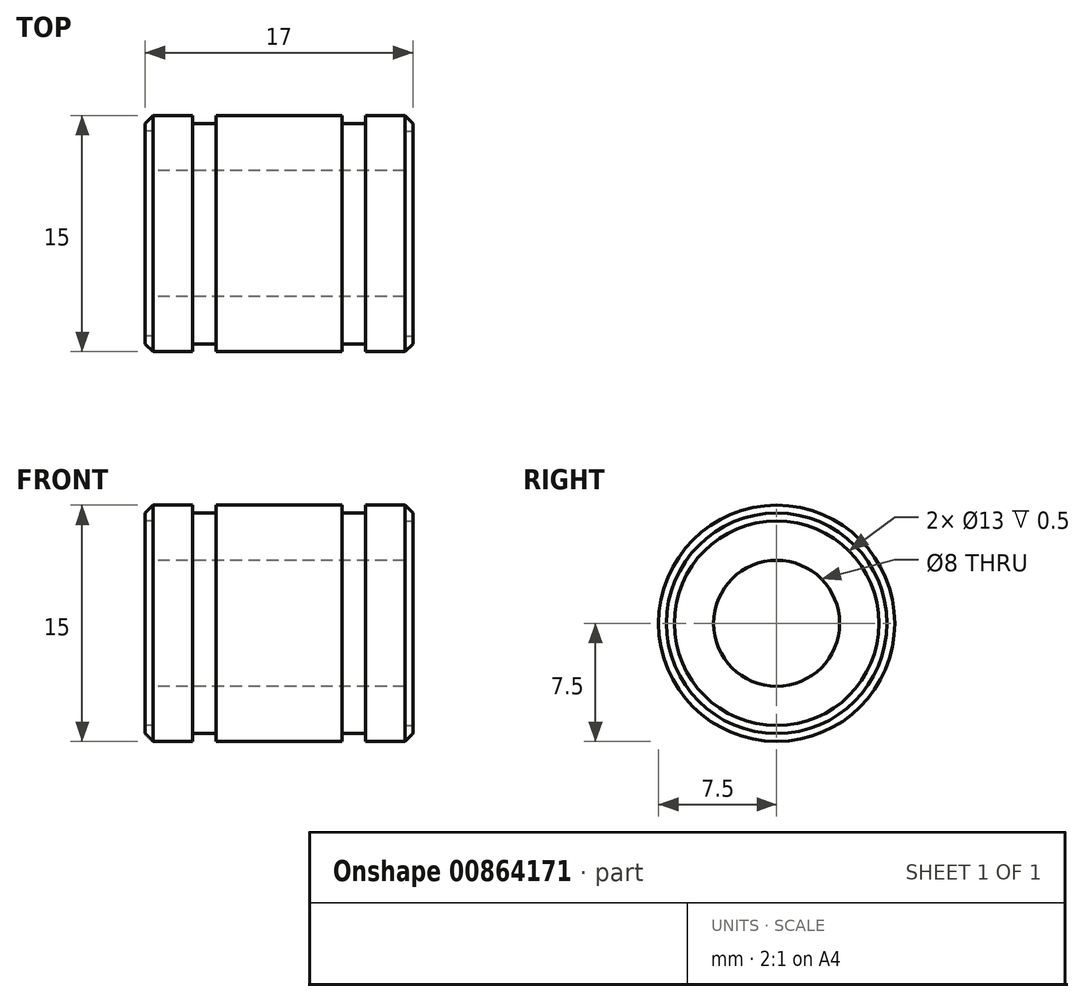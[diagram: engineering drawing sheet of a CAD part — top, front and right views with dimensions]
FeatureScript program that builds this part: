
annotation { "Feature Type Name" : "Feature", "Feature Type Description" : "" }
export const myFeature = defineFeature(function(context is Context, id is Id, definition is map)
    precondition{}
    {
        {
            var Q0;
            Q0=qCreatedBy(makeId("Right.planeOp"),FACE);
            var sketch = newSketch(context, id + "F0", { "sketchPlane" : qUnion([Q0])});
            skCircle(sketch, "E0", {"center": v(0, 0) * mm, "radius": 4 * mm});
            skCircle(sketch, "E1", {"center": v(0, 0) * mm, "radius": 7.5 * mm});
            skSolve(sketch);
        }
        {
            var Q0;
            Q0 = qSketchRegion(id + "F0", true);
            extrude(context, id + "F1", {"entities" : qUnion([Q0]), "endBound" : BoundingType.SYMMETRIC, "depth" : 17 * mm, "offsetDistance" : 25 * mm});
        }
        {
            var Q0;
            Q0=makeQuery(id+"F1.opExtrude","CAP_FACE",FACE,{"disambiguationData":[OSD([sQuery(id+"F0.wireOp",EDGE,"E0"),sQuery(id+"F0.wireOp",EDGE,"E1")])],"isStart":false});
            var sketch = newSketch(context, id + "F2", { "sketchPlane" : qUnion([Q0])});
            skCircle(sketch, "E2", {"center": v(0, 0) * mm, "radius": 6.5 * mm});
            skSolve(sketch);
        }
        {
            var Q0;
            Q0 = qSketchRegion(id + "F2", true);
            extrude(context, id + "F3", {"entities" : qUnion([Q0]), "operationType" : NewBodyOperationType.REMOVE, "oppositeDirection" : true, "depth" : .5 * mm, "offsetDistance" : 25 * mm});
        }
        {
            var Q0;
            Q0=makeQuery(id+"F1.opExtrude","CAP_FACE",FACE,{"disambiguationData":[OSD([sQuery(id+"F0.wireOp",EDGE,"E0"),sQuery(id+"F0.wireOp",EDGE,"E1")])],"isStart":true});
            var sketch = newSketch(context, id + "F4", { "sketchPlane" : qUnion([Q0])});
            skCircle(sketch, "E3", {"center": v(0, 0) * mm, "radius": 6.5 * mm});
            skSolve(sketch);
        }
        {
            var Q0;
            Q0 = qSketchRegion(id + "F4", true);
            extrude(context, id + "F5", {"entities" : qUnion([Q0]), "operationType" : NewBodyOperationType.REMOVE, "oppositeDirection" : true, "depth" : .5 * mm, "offsetDistance" : 25 * mm});
        }
        {
            var Q0;
            Q0=qCreatedBy(makeId("Front.planeOp"),FACE);
            var sketch = newSketch(context, id + "F6", { "sketchPlane" : qUnion([Q0])});
            skLineSegment(sketch, "E4.bottom", {"start": v(-5.5, 8) * mm, "end": v(-4, 8) * mm});
            skLineSegment(sketch, "E4.top", {"start": v(-5.5, 7) * mm, "end": v(-4, 7) * mm});
            skLineSegment(sketch, "E4.left", {"start": v(-5.5, 8) * mm, "end": v(-5.5, 7) * mm});
            skLineSegment(sketch, "E4.right", {"start": v(-4, 8) * mm, "end": v(-4, 7) * mm});
            skLineSegment(sketch, "E5.bottom", {"start": v(4, 8) * mm, "end": v(5.5, 8) * mm});
            skLineSegment(sketch, "E5.top", {"start": v(4, 7) * mm, "end": v(5.5, 7) * mm});
            skLineSegment(sketch, "E5.left", {"start": v(4, 8) * mm, "end": v(4, 7) * mm});
            skLineSegment(sketch, "E5.right", {"start": v(5.5, 8) * mm, "end": v(5.5, 7) * mm});
            skLineSegment(sketch, "E6", {"start": v(-5.5, 7) * mm, "end": v(-5.5, 0) * mm, "construction": true});
            skLineSegment(sketch, "E7", {"start": v(-5.5, 0) * mm, "end": v(5.5, 0) * mm, "construction": true});
            skLineSegment(sketch, "E8", {"start": v(5.5, 0) * mm, "end": v(5.5, 7) * mm, "construction": true});
            skSolve(sketch);
        }
        {
            var Q0;
            Q0 = qSketchRegion(id + "F6", true);
            var Q1;
            Q1=sQuery(id+"F6.wireOp",EDGE,"E7");
            revolve(context, id + "F7", {"operationType" : NewBodyOperationType.REMOVE, "surfaceOperationType" : NewSurfaceOperationType.NEW, "entities" : qUnion([Q0]), "axis" : qUnion([Q1]), "revolveType" : RevolveType.FULL, "oppositeDirection" : true});
        }
        {
            var Q0;
            Q0=makeQuery(id+"F1.opExtrude","CAP_EDGE",EDGE,{"disambiguationData":[OSD([sQuery(id+"F0.wireOp",EDGE,"E1")])],"isStart":true});
            var Q1;
            Q1=makeQuery(id+"F1.opExtrude","CAP_EDGE",EDGE,{"disambiguationData":[OSD([sQuery(id+"F0.wireOp",EDGE,"E1")])],"isStart":false});
            chamfer(context, id + "F8", {"entities" : qUnion([Q0, Q1]), "width" : .5 * mm, "tangentPropagation" : true});
        }
    });
